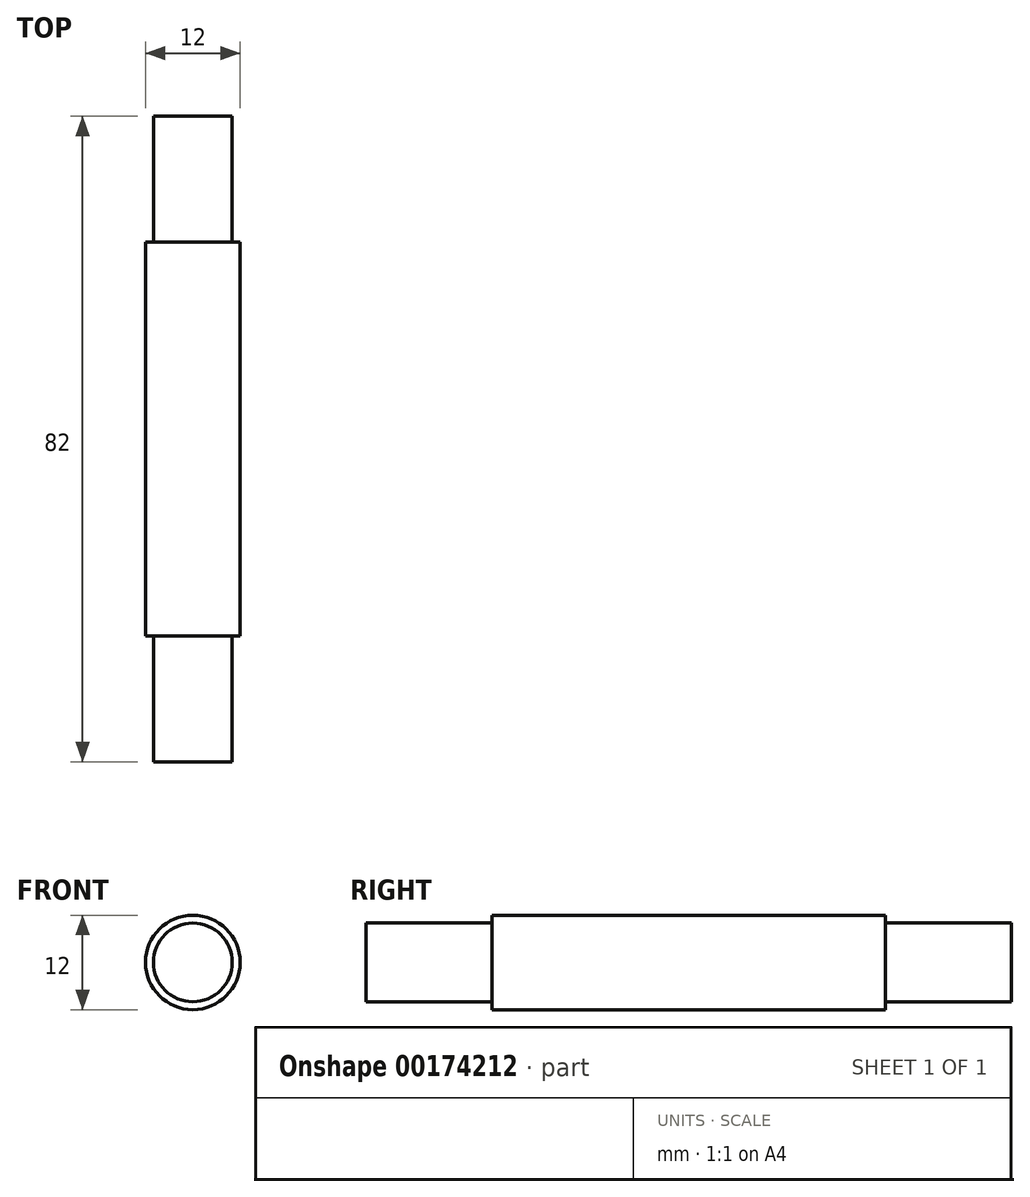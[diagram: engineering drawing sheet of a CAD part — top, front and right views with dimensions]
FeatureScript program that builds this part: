
annotation { "Feature Type Name" : "Feature", "Feature Type Description" : "" }
export const myFeature = defineFeature(function(context is Context, id is Id, definition is map)
    precondition{}
    {
        {
            var Q0;
            Q0=qCreatedBy(makeId("Right.planeOp"),FACE);
            var sketch = newSketch(context, id + "F0", { "sketchPlane" : qUnion([Q0])});
            skLineSegment(sketch, "E0", {"start": v(0, 0) * mm, "end": v(82, 0) * mm, "construction": true});
            skLineSegment(sketch, "E1", {"start": v(0, 0) * mm, "end": v(0, -5) * mm});
            skLineSegment(sketch, "E2", {"start": v(0, -5) * mm, "end": v(16, -5) * mm});
            skLineSegment(sketch, "E3", {"start": v(16, -5) * mm, "end": v(16, -6) * mm});
            skLineSegment(sketch, "E4", {"start": v(16, -6) * mm, "end": v(66, -6) * mm});
            skLineSegment(sketch, "E5", {"start": v(66, -6) * mm, "end": v(66, -5) * mm});
            skLineSegment(sketch, "E6", {"start": v(66, -5) * mm, "end": v(82, -5) * mm});
            skLineSegment(sketch, "E7", {"start": v(82, -5) * mm, "end": v(82, 0) * mm});
            skLineSegment(sketch, "E8", {"start": v(0, 0) * mm, "end": v(82, 0) * mm});
            skSolve(sketch);
        }
        {
            var Q0;
            Q0 = qSketchRegion(id + "F0", true);
            var Q1;
            Q1=sQuery(id+"F0.wireOp",EDGE,"E8");
            revolve(context, id + "F1", {"entities" : qUnion([Q0]), "axis" : qUnion([Q1]), "revolveType" : RevolveType.FULL});
        }
    });
